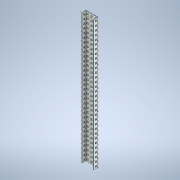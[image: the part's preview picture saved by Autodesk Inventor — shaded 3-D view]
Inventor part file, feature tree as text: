
AUTODESK INVENTOR PART (.ipt)
format: ipt  version: 2020 (Build 240168000, 168)  size: 1,455,616 bytes
history: native  units: in
note: dims shown in document units (in); Inventor stores cm internally (conversion verified against a paired STEP export)
features: other x163, plane x5, pattern_linear x3, split x1, sheet_metal_op x1
ambient origin geometry x8: Origin, YZ Plane, XZ Plane, XY Plane, X Axis, Y Axis, Z Axis, Center Point
bodies: Solid1 (feature_tree)
feature tree (173):
  plane  "Work Plane2"
  plane  "Work Plane1"
  other  "Work Point1"
  other  "Work Point2"
  other  "Work Axis1"
  other  "Work Axis2"
  other  "Work Axis3"
  pattern_linear  "Rectangular Pattern1"  Count1=32 Spacing1=0.5in
  pattern_linear  "Rectangular Pattern2"  Count1=32 Spacing1=0.5in
  pattern_linear  "Rectangular Pattern3"  Count1=32 Spacing1=0.5in
  plane  "Work Plane5"
  split  "Split1"
  plane  "Work Plane3"
  plane  "Work Plane4"
  other  "Work Point3"
  other  "Work Axis4"
  other  "Work Axis5"
  other  "Work Axis6"
  other  "Work Axis7"
  other  "Work Axis8"
  other  "Work Axis9"
  other  "Work Axis10"
  other  "Work Axis11"
  other  "Work Axis12"
  other  "Work Axis13"
  other  "Work Axis14"
  other  "Work Axis15"
  other  "Work Axis16"
  other  "Work Axis17"
  other  "Work Axis18"
  other  "Work Axis19"
  other  "Work Axis20"
  other  "Work Axis21"
  other  "Work Axis22"
  other  "Work Axis23"
  other  "Work Axis24"
  other  "Work Axis25"
  other  "Work Axis26"
  other  "Work Axis27"
  other  "Work Axis28"
  other  "Work Axis29"
  other  "Work Axis30"
  other  "Work Axis31"
  other  "Work Axis32"
  other  "Work Axis33"
  other  "Work Axis34"
  other  "Work Axis38"
  other  "Work Axis39"
  other  "Work Axis40"
  other  "Work Axis41"
  other  "Work Axis42"
  other  "Work Axis43"
  other  "Work Axis44"
  other  "Work Axis45"
  other  "Work Axis46"
  other  "Work Axis47"
  other  "Work Axis48"
  other  "Work Axis49"
  other  "Work Axis50"
  other  "Work Axis51"
  other  "Work Axis52"
  other  "Work Axis53"
  other  "Work Axis54"
  other  "Work Axis55"
  other  "Work Axis56"
  other  "Work Axis57"
  other  "Work Axis58"
  other  "Work Axis59"
  other  "Work Axis60"
  other  "Work Axis61"
  other  "Work Axis62"
  other  "Work Axis63"
  other  "Work Axis64"
  other  "Work Axis65"
  other  "Work Axis66"
  other  "Work Axis67"
  other  "Work Axis68"
  other  "Work Axis72"
  other  "Work Axis73"
  other  "Work Axis74"
  other  "Work Axis75"
  other  "Work Axis76"
  other  "Work Axis77"
  other  "Work Axis78"
  other  "Work Axis79"
  other  "Work Axis80"
  other  "Work Axis81"
  other  "Work Axis82"
  other  "Work Axis83"
  other  "Work Axis84"
  other  "Work Axis85"
  other  "Work Axis86"
  other  "Work Axis87"
  other  "Work Axis88"
  other  "Work Axis89"
  other  "Work Axis90"
  other  "Work Axis91"
  other  "Work Axis92"
  other  "Work Axis93"
  other  "Work Axis94"
  other  "Work Axis95"
  other  "Work Axis96"
  other  "Work Axis97"
  other  "Work Axis98"
  other  "Work Axis99"
  other  "Work Axis100"
  other  "Work Axis101"
  other  "Work Axis102"
  other  "Work Axis106"
  other  "Work Axis107"
  other  "Work Axis108"
  other  "Work Axis109"
  other  "Work Axis110"
  other  "Work Axis111"
  other  "Work Axis112"
  other  "Work Axis113"
  other  "Work Axis114"
  other  "Work Axis115"
  other  "Work Axis116"
  other  "Work Axis117"
  other  "Work Axis118"
  other  "Work Axis119"
  other  "Work Axis120"
  other  "Work Axis121"
  other  "Work Axis122"
  other  "Work Axis123"
  other  "Work Axis124"
  other  "Work Axis125"
  other  "Work Axis126"
  other  "Work Axis127"
  other  "Work Axis128"
  other  "Work Axis129"
  other  "Work Axis130"
  other  "Work Axis131"
  other  "Work Axis132"
  other  "Work Axis133"
  other  "Work Axis134"
  other  "Work Axis135"
  other  "Work Axis136"
  other  "Work Axis137"
  other  "Work Axis141"
  other  "Work Axis142"
  other  "Work Axis143"
  other  "Work Axis144"
  other  "Work Axis145"
  other  "Work Axis146"
  other  "Work Axis147"
  other  "Work Axis148"
  other  "Work Axis149"
  other  "Work Axis150"
  other  "Work Axis151"
  other  "Work Axis152"
  other  "Work Axis153"
  other  "Work Axis154"
  other  "Work Axis155"
  other  "Work Axis156"
  other  "Work Axis157"
  other  "Work Axis158"
  other  "Work Axis159"
  other  "Work Axis160"
  other  "Work Axis161"
  other  "Work Axis162"
  other  "Work Axis163"
  other  "Work Axis164"
  other  "Work Axis165"
  other  "Work Axis166"
  other  "Work Axis167"
  other  "Work Axis168"
  other  "Work Axis169"
  other  "Work Axis170"
  other  "Work Axis171"
  other  "Work Axis172"
  sheet_metal_op  "Fold1"
